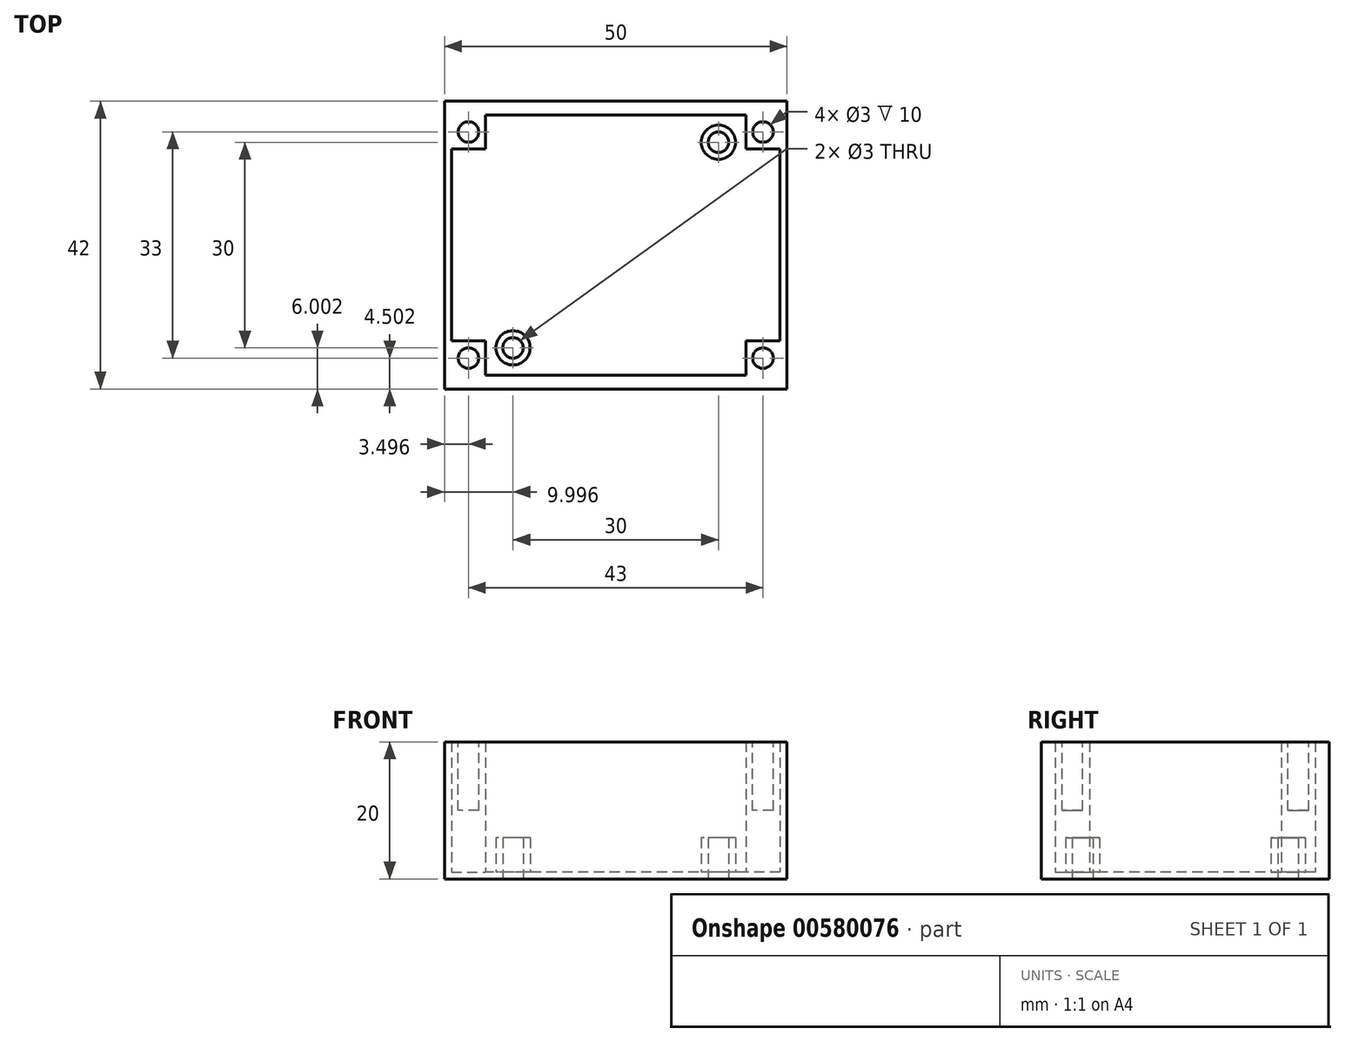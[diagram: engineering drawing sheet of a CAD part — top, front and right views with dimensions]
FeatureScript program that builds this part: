
annotation { "Feature Type Name" : "Feature", "Feature Type Description" : "" }
export const myFeature = defineFeature(function(context is Context, id is Id, definition is map)
    precondition{}
    {
        {
            var Q0;
            Q0=qCreatedBy(makeId("Top.planeOp"),FACE);
            var sketch = newSketch(context, id + "F0", { "sketchPlane" : qUnion([Q0])});
            skLineSegment(sketch, "E0.bottom", {"start": v(-62.05, 63.24) * mm, "end": v(-12.05, 63.24) * mm});
            skLineSegment(sketch, "E0.top", {"start": v(-62.05, 21.24) * mm, "end": v(-12.05, 21.24) * mm});
            skLineSegment(sketch, "E0.left", {"start": v(-62.05, 63.24) * mm, "end": v(-62.05, 21.24) * mm});
            skLineSegment(sketch, "E0.right", {"start": v(-12.05, 63.24) * mm, "end": v(-12.05, 21.24) * mm});
            skSolve(sketch);
        }
        {
            var Q0;
            Q0=makeQuery(id+"F0.imprint","IMPRINT",FACE,{"disambiguationData":[TD([[makeQuery(id+"F0.imprint","IMPRINT",EDGE,{"derivedFrom":sQuery(id+"F0.wireOp",EDGE,"E0.bottom")}),-1.0]])]});
            extrude(context, id + "F1", {"entities" : qUnion([Q0]), "depth" : 20 * mm, "offsetDistance" : 25 * mm});
        }
        {
            var Q0;
            Q0=makeQuery(id+"F1.opExtrude","CAP_FACE",FACE,{"disambiguationData":[OSD([sQuery(id+"F0.wireOp",EDGE,"E0.bottom"),sQuery(id+"F0.wireOp",EDGE,"E0.top"),sQuery(id+"F0.wireOp",EDGE,"E0.left"),sQuery(id+"F0.wireOp",EDGE,"E0.right")])],"isStart":false});
            var sketch = newSketch(context, id + "F2", { "sketchPlane" : qUnion([Q0])});
            skLineSegment(sketch, "E1.bottom", {"start": v(-18.05, 23.24) * mm, "end": v(-56.05, 23.24) * mm});
            skLineSegment(sketch, "E1.top", {"start": v(-18.05, 61.24) * mm, "end": v(-56.05, 61.24) * mm});
            skLineSegment(sketch, "E1.left", {"start": v(-18.05, 23.24) * mm, "end": v(-18.05, 61.24) * mm});
            skLineSegment(sketch, "E1.right", {"start": v(-56.05, 23.24) * mm, "end": v(-56.05, 61.24) * mm});
            skPoint(sketch, "E1.middle", {"position": v(-37.05, 42.24) * mm});
            skPoint(sketch, "E1.middle.positionSnap0", {"position": v(-37.05, 63.24) * mm});
            skPoint(sketch, "E1.middle.positionSnap1", {"position": v(-12.05, 42.24) * mm});
            skPoint(sketch, "E1.centerSnap0", {"position": v(-37.05, 63.24) * mm});
            skPoint(sketch, "E1.centerSnap1", {"position": v(-12.05, 42.24) * mm});
            skSolve(sketch);
        }
        {
            var Q0;
            Q0=makeQuery(id+"F2.imprint","IMPRINT",FACE,{"disambiguationData":[TD([[makeQuery(id+"F2.imprint","IMPRINT",EDGE,{"derivedFrom":sQuery(id+"F2.wireOp",EDGE,"E1.bottom")}),-1.0]])]});
            extrude(context, id + "F3", {"entities" : qUnion([Q0]), "operationType" : NewBodyOperationType.REMOVE, "oppositeDirection" : true, "depth" : 19 * mm, "offsetDistance" : 25 * mm});
        }
        {
            var Q0;
            Q0=makeQuery(id+"F1.opExtrude","CAP_FACE",FACE,{"disambiguationData":[OSD([sQuery(id+"F0.wireOp",EDGE,"E0.bottom"),sQuery(id+"F0.wireOp",EDGE,"E0.top"),sQuery(id+"F0.wireOp",EDGE,"E0.left"),sQuery(id+"F0.wireOp",EDGE,"E0.right")])],"isStart":false});
            var sketch = newSketch(context, id + "F4", { "sketchPlane" : qUnion([Q0])});
            skLineSegment(sketch, "E2.bottom", {"start": v(-18.05, 61.24) * mm, "end": v(-13.05, 61.24) * mm});
            skLineSegment(sketch, "E2.top", {"start": v(-18.05, 23.24) * mm, "end": v(-13.05, 23.24) * mm});
            skLineSegment(sketch, "E2.left", {"start": v(-18.05, 61.24) * mm, "end": v(-18.05, 23.24) * mm});
            skLineSegment(sketch, "E2.right", {"start": v(-13.05, 61.24) * mm, "end": v(-13.05, 23.24) * mm});
            skLineSegment(sketch, "E3.bottom", {"start": v(-56.05, 61.24) * mm, "end": v(-61.05, 61.24) * mm});
            skLineSegment(sketch, "E3.top", {"start": v(-56.05, 23.24) * mm, "end": v(-61.05, 23.24) * mm});
            skLineSegment(sketch, "E3.left", {"start": v(-56.05, 61.24) * mm, "end": v(-56.05, 23.24) * mm});
            skLineSegment(sketch, "E3.right", {"start": v(-61.05, 61.24) * mm, "end": v(-61.05, 23.24) * mm});
            skSolve(sketch);
        }
        {
            var Q0;
            Q0=makeQuery(id+"F4.imprint","IMPRINT",FACE,{"disambiguationData":[TD([[makeQuery(id+"F4.imprint","IMPRINT",EDGE,{"derivedFrom":sQuery(id+"F4.wireOp",EDGE,"E2.bottom")}),-1.0]])]});
            var Q1;
            Q1=makeQuery(id+"F4.imprint","IMPRINT",FACE,{"disambiguationData":[TD([[makeQuery(id+"F4.imprint","IMPRINT",EDGE,{"derivedFrom":sQuery(id+"F4.wireOp",EDGE,"E3.bottom")}),1.0]])]});
            extrude(context, id + "F5", {"entities" : qUnion([Q0, Q1]), "operationType" : NewBodyOperationType.REMOVE, "oppositeDirection" : true, "depth" : 19 * mm, "offsetDistance" : 25 * mm});
        }
        {
            var Q0;
            Q0=makeQuery(id+"F5.boolean.opBoolean","MERGE",FACE,{"derivedFrom":[makeQuery(id+"F3.boolean.opBoolean","COPY",FACE,{"derivedFrom":makeQuery(id+"F3.opExtrude","CAP_FACE",FACE,{"disambiguationData":[OSD([sQuery(id+"F2.wireOp",EDGE,"E1.bottom"),sQuery(id+"F2.wireOp",EDGE,"E1.top"),sQuery(id+"F2.wireOp",EDGE,"E1.left"),sQuery(id+"F2.wireOp",EDGE,"E1.right")])],"isStart":false})}),makeQuery(id+"F5.opExtrude","CAP_FACE",FACE,{"disambiguationData":[OSD([sQuery(id+"F4.wireOp",EDGE,"E2.bottom"),sQuery(id+"F4.wireOp",EDGE,"E2.top"),sQuery(id+"F4.wireOp",EDGE,"E2.left"),sQuery(id+"F4.wireOp",EDGE,"E2.right")])],"isStart":false}),makeQuery(id+"F5.opExtrude","CAP_FACE",FACE,{"disambiguationData":[OSD([sQuery(id+"F4.wireOp",EDGE,"E3.bottom"),sQuery(id+"F4.wireOp",EDGE,"E3.top"),sQuery(id+"F4.wireOp",EDGE,"E3.left"),sQuery(id+"F4.wireOp",EDGE,"E3.right")])],"isStart":false})]});
            var sketch = newSketch(context, id + "F6", { "sketchPlane" : qUnion([Q0])});
            skLineSegment(sketch, "E4.bottom", {"start": v(-13.05, 23.24) * mm, "end": v(-18.05, 23.24) * mm});
            skLineSegment(sketch, "E4.top", {"start": v(-13.05, 28.24) * mm, "end": v(-18.05, 28.24) * mm});
            skLineSegment(sketch, "E4.left", {"start": v(-13.05, 23.24) * mm, "end": v(-13.05, 28.24) * mm});
            skLineSegment(sketch, "E4.right", {"start": v(-18.05, 23.24) * mm, "end": v(-18.05, 28.24) * mm});
            skLineSegment(sketch, "E5.bottom", {"start": v(-61.05, 23.24) * mm, "end": v(-56.05, 23.24) * mm});
            skLineSegment(sketch, "E5.top", {"start": v(-61.05, 28.24) * mm, "end": v(-56.05, 28.24) * mm});
            skLineSegment(sketch, "E5.left", {"start": v(-61.05, 23.24) * mm, "end": v(-61.05, 28.24) * mm});
            skLineSegment(sketch, "E5.right", {"start": v(-56.05, 23.24) * mm, "end": v(-56.05, 28.24) * mm});
            skLineSegment(sketch, "E6.bottom", {"start": v(-13.05, 61.24) * mm, "end": v(-18.05, 61.24) * mm});
            skLineSegment(sketch, "E6.top", {"start": v(-13.05, 56.24) * mm, "end": v(-18.05, 56.24) * mm});
            skLineSegment(sketch, "E6.left", {"start": v(-13.05, 61.24) * mm, "end": v(-13.05, 56.24) * mm});
            skLineSegment(sketch, "E6.right", {"start": v(-18.05, 61.24) * mm, "end": v(-18.05, 56.24) * mm});
            skLineSegment(sketch, "E7.bottom", {"start": v(-61.05, 61.24) * mm, "end": v(-56.05, 61.24) * mm});
            skLineSegment(sketch, "E7.top", {"start": v(-61.05, 56.24) * mm, "end": v(-56.05, 56.24) * mm});
            skLineSegment(sketch, "E7.left", {"start": v(-61.05, 61.24) * mm, "end": v(-61.05, 56.24) * mm});
            skLineSegment(sketch, "E7.right", {"start": v(-56.05, 61.24) * mm, "end": v(-56.05, 56.24) * mm});
            skSolve(sketch);
        }
        {
            var Q0;
            Q0=makeQuery(id+"F6.imprint","IMPRINT",FACE,{"disambiguationData":[TD([[makeQuery(id+"F6.imprint","IMPRINT",EDGE,{"derivedFrom":sQuery(id+"F6.wireOp",EDGE,"E6.bottom")}),1.0]])]});
            var Q1;
            Q1=makeQuery(id+"F6.imprint","IMPRINT",FACE,{"disambiguationData":[TD([[makeQuery(id+"F6.imprint","IMPRINT",EDGE,{"derivedFrom":sQuery(id+"F6.wireOp",EDGE,"E4.bottom")}),-1.0]])]});
            var Q2;
            Q2=makeQuery(id+"F6.imprint","IMPRINT",FACE,{"disambiguationData":[TD([[makeQuery(id+"F6.imprint","IMPRINT",EDGE,{"derivedFrom":sQuery(id+"F6.wireOp",EDGE,"E7.bottom")}),1.0]])]});
            var Q3;
            Q3=makeQuery(id+"F6.imprint","IMPRINT",FACE,{"disambiguationData":[TD([[makeQuery(id+"F6.imprint","IMPRINT",EDGE,{"derivedFrom":sQuery(id+"F6.wireOp",EDGE,"E5.bottom")}),-1.0]])]});
            extrude(context, id + "F7", {"entities" : qUnion([Q0, Q1, Q2, Q3]), "operationType" : NewBodyOperationType.ADD, "depth" : 19 * mm, "offsetDistance" : 25 * mm});
        }
        {
            var Q0;
            Q0=makeQuery(id+"F7.boolean.opBoolean","MERGE",FACE,{"derivedFrom":[makeQuery(id+"F1.opExtrude","CAP_FACE",FACE,{"disambiguationData":[OSD([sQuery(id+"F0.wireOp",EDGE,"E0.bottom"),sQuery(id+"F0.wireOp",EDGE,"E0.top"),sQuery(id+"F0.wireOp",EDGE,"E0.left"),sQuery(id+"F0.wireOp",EDGE,"E0.right")])],"isStart":false}),makeQuery(id+"F7.opExtrude","CAP_FACE",FACE,{"disambiguationData":[OSD([sQuery(id+"F6.wireOp",EDGE,"E4.bottom"),sQuery(id+"F6.wireOp",EDGE,"E4.top"),sQuery(id+"F6.wireOp",EDGE,"E4.left"),sQuery(id+"F6.wireOp",EDGE,"E4.right")])],"isStart":false}),makeQuery(id+"F7.opExtrude","CAP_FACE",FACE,{"disambiguationData":[OSD([sQuery(id+"F6.wireOp",EDGE,"E5.bottom"),sQuery(id+"F6.wireOp",EDGE,"E5.top"),sQuery(id+"F6.wireOp",EDGE,"E5.left"),sQuery(id+"F6.wireOp",EDGE,"E5.right")])],"isStart":false}),makeQuery(id+"F7.opExtrude","CAP_FACE",FACE,{"disambiguationData":[OSD([sQuery(id+"F6.wireOp",EDGE,"E6.bottom"),sQuery(id+"F6.wireOp",EDGE,"E6.top"),sQuery(id+"F6.wireOp",EDGE,"E6.left"),sQuery(id+"F6.wireOp",EDGE,"E6.right")])],"isStart":false}),makeQuery(id+"F7.opExtrude","CAP_FACE",FACE,{"disambiguationData":[OSD([sQuery(id+"F6.wireOp",EDGE,"E7.bottom"),sQuery(id+"F6.wireOp",EDGE,"E7.top"),sQuery(id+"F6.wireOp",EDGE,"E7.left"),sQuery(id+"F6.wireOp",EDGE,"E7.right")])],"isStart":false})]});
            var sketch = newSketch(context, id + "F8", { "sketchPlane" : qUnion([Q0])});
            skCircle(sketch, "E8", {"center": v(-58.55, 58.74) * mm, "radius": 1.5 * mm});
            skPoint(sketch, "E8.centerSnap0", {"position": v(-58.55, 56.24) * mm});
            skPoint(sketch, "E8.centerSnap1", {"position": v(-56.05, 58.74) * mm});
            skCircle(sketch, "E9", {"center": v(-58.55, 25.74) * mm, "radius": 1.5 * mm});
            skPoint(sketch, "E9.centerSnap0", {"position": v(-56.05, 25.74) * mm});
            skPoint(sketch, "E9.centerSnap1", {"position": v(-58.55, 28.24) * mm});
            skCircle(sketch, "E10", {"center": v(-15.55, 25.74) * mm, "radius": 1.5 * mm});
            skPoint(sketch, "E10.centerSnap0", {"position": v(-18.05, 25.74) * mm});
            skPoint(sketch, "E10.centerSnap1", {"position": v(-15.55, 28.24) * mm});
            skCircle(sketch, "E11", {"center": v(-15.55, 58.74) * mm, "radius": 1.5 * mm});
            skPoint(sketch, "E11.centerSnap0", {"position": v(-15.55, 56.24) * mm});
            skPoint(sketch, "E11.centerSnap1", {"position": v(-18.05, 58.74) * mm});
            skSolve(sketch);
        }
        {
            var Q0;
            Q0=makeQuery(id+"F8.imprint","IMPRINT",FACE,{"disambiguationData":[TD([[makeQuery(id+"F8.imprint","IMPRINT",EDGE,{"derivedFrom":sQuery(id+"F8.wireOp",EDGE,"E11")}),1.0]])]});
            var Q1;
            Q1=makeQuery(id+"F8.imprint","IMPRINT",FACE,{"disambiguationData":[TD([[makeQuery(id+"F8.imprint","IMPRINT",EDGE,{"derivedFrom":sQuery(id+"F8.wireOp",EDGE,"E10")}),1.0]])]});
            var Q2;
            Q2=makeQuery(id+"F8.imprint","IMPRINT",FACE,{"disambiguationData":[TD([[makeQuery(id+"F8.imprint","IMPRINT",EDGE,{"derivedFrom":sQuery(id+"F8.wireOp",EDGE,"E9")}),1.0]])]});
            var Q3;
            Q3=makeQuery(id+"F8.imprint","IMPRINT",FACE,{"disambiguationData":[TD([[makeQuery(id+"F8.imprint","IMPRINT",EDGE,{"derivedFrom":sQuery(id+"F8.wireOp",EDGE,"E8")}),1.0]])]});
            extrude(context, id + "F9", {"entities" : qUnion([Q0, Q1, Q2, Q3]), "operationType" : NewBodyOperationType.REMOVE, "oppositeDirection" : true, "depth" : 10 * mm, "offsetDistance" : 25 * mm});
        }
        {
            var Q0;
            Q0=makeQuery(id+"F5.boolean.opBoolean","MERGE",FACE,{"derivedFrom":[makeQuery(id+"F3.boolean.opBoolean","COPY",FACE,{"derivedFrom":makeQuery(id+"F3.opExtrude","CAP_FACE",FACE,{"disambiguationData":[OSD([sQuery(id+"F2.wireOp",EDGE,"E1.bottom"),sQuery(id+"F2.wireOp",EDGE,"E1.top"),sQuery(id+"F2.wireOp",EDGE,"E1.left"),sQuery(id+"F2.wireOp",EDGE,"E1.right")])],"isStart":false})}),makeQuery(id+"F5.opExtrude","CAP_FACE",FACE,{"disambiguationData":[OSD([sQuery(id+"F4.wireOp",EDGE,"E2.bottom"),sQuery(id+"F4.wireOp",EDGE,"E2.top"),sQuery(id+"F4.wireOp",EDGE,"E2.left"),sQuery(id+"F4.wireOp",EDGE,"E2.right")])],"isStart":false}),makeQuery(id+"F5.opExtrude","CAP_FACE",FACE,{"disambiguationData":[OSD([sQuery(id+"F4.wireOp",EDGE,"E3.bottom"),sQuery(id+"F4.wireOp",EDGE,"E3.top"),sQuery(id+"F4.wireOp",EDGE,"E3.left"),sQuery(id+"F4.wireOp",EDGE,"E3.right")])],"isStart":false})]});
            var sketch = newSketch(context, id + "F10", { "sketchPlane" : qUnion([Q0])});
            skCircle(sketch, "E12", {"center": v(-52.05, 27.24) * mm, "radius": 2.5 * mm});
            skCircle(sketch, "E13", {"center": v(-22.05, 57.24) * mm, "radius": 2.5 * mm});
            skCircle(sketch, "E14", {"center": v(-52.05, 27.24) * mm, "radius": 1.5 * mm});
            skCircle(sketch, "E15", {"center": v(-22.05, 57.24) * mm, "radius": 1.5 * mm});
            skSolve(sketch);
        }
        {
            var Q0;
            Q0=makeQuery(id+"F10.imprint","IMPRINT",FACE,{"disambiguationData":[TD([[makeQuery(id+"F10.imprint","IMPRINT",EDGE,{"derivedFrom":sQuery(id+"F10.wireOp",EDGE,"E13")}),1.0]])]});
            var Q1;
            Q1=makeQuery(id+"F10.imprint","IMPRINT",FACE,{"disambiguationData":[TD([[makeQuery(id+"F10.imprint","IMPRINT",EDGE,{"derivedFrom":sQuery(id+"F10.wireOp",EDGE,"E12")}),1.0]])]});
            extrude(context, id + "F11", {"entities" : qUnion([Q0, Q1]), "operationType" : NewBodyOperationType.ADD, "depth" : 5 * mm, "offsetDistance" : 25 * mm});
        }
        {
            var Q0;
            Q0=makeQuery(id+"F11.boolean.opBoolean","SPLIT",FACE,{"disambiguationData":[TD([makeQuery(id+"F11.opExtrude","SWEPT_FACE",FACE,{"disambiguationData":[OSD([sQuery(id+"F10.wireOp",EDGE,"E15")])]})])],"derivedFrom":makeQuery(id+"F5.boolean.opBoolean","MERGE",FACE,{"derivedFrom":[makeQuery(id+"F3.boolean.opBoolean","COPY",FACE,{"derivedFrom":makeQuery(id+"F3.opExtrude","CAP_FACE",FACE,{"disambiguationData":[OSD([sQuery(id+"F2.wireOp",EDGE,"E1.bottom"),sQuery(id+"F2.wireOp",EDGE,"E1.top"),sQuery(id+"F2.wireOp",EDGE,"E1.left"),sQuery(id+"F2.wireOp",EDGE,"E1.right")])],"isStart":false})}),makeQuery(id+"F5.opExtrude","CAP_FACE",FACE,{"disambiguationData":[OSD([sQuery(id+"F4.wireOp",EDGE,"E2.bottom"),sQuery(id+"F4.wireOp",EDGE,"E2.top"),sQuery(id+"F4.wireOp",EDGE,"E2.left"),sQuery(id+"F4.wireOp",EDGE,"E2.right")])],"isStart":false}),makeQuery(id+"F5.opExtrude","CAP_FACE",FACE,{"disambiguationData":[OSD([sQuery(id+"F4.wireOp",EDGE,"E3.bottom"),sQuery(id+"F4.wireOp",EDGE,"E3.top"),sQuery(id+"F4.wireOp",EDGE,"E3.left"),sQuery(id+"F4.wireOp",EDGE,"E3.right")])],"isStart":false})]})});
            var Q1;
            Q1=makeQuery(id+"F11.boolean.opBoolean","SPLIT",FACE,{"disambiguationData":[TD([makeQuery(id+"F11.opExtrude","SWEPT_FACE",FACE,{"disambiguationData":[OSD([sQuery(id+"F10.wireOp",EDGE,"E14")])]})])],"derivedFrom":makeQuery(id+"F5.boolean.opBoolean","MERGE",FACE,{"derivedFrom":[makeQuery(id+"F3.boolean.opBoolean","COPY",FACE,{"derivedFrom":makeQuery(id+"F3.opExtrude","CAP_FACE",FACE,{"disambiguationData":[OSD([sQuery(id+"F2.wireOp",EDGE,"E1.bottom"),sQuery(id+"F2.wireOp",EDGE,"E1.top"),sQuery(id+"F2.wireOp",EDGE,"E1.left"),sQuery(id+"F2.wireOp",EDGE,"E1.right")])],"isStart":false})}),makeQuery(id+"F5.opExtrude","CAP_FACE",FACE,{"disambiguationData":[OSD([sQuery(id+"F4.wireOp",EDGE,"E2.bottom"),sQuery(id+"F4.wireOp",EDGE,"E2.top"),sQuery(id+"F4.wireOp",EDGE,"E2.left"),sQuery(id+"F4.wireOp",EDGE,"E2.right")])],"isStart":false}),makeQuery(id+"F5.opExtrude","CAP_FACE",FACE,{"disambiguationData":[OSD([sQuery(id+"F4.wireOp",EDGE,"E3.bottom"),sQuery(id+"F4.wireOp",EDGE,"E3.top"),sQuery(id+"F4.wireOp",EDGE,"E3.left"),sQuery(id+"F4.wireOp",EDGE,"E3.right")])],"isStart":false})]})});
            extrude(context, id + "F12", {"entities" : qUnion([Q0, Q1]), "operationType" : NewBodyOperationType.REMOVE, "oppositeDirection" : true, "depth" : 1 * mm, "offsetDistance" : 25 * mm});
        }
    });
